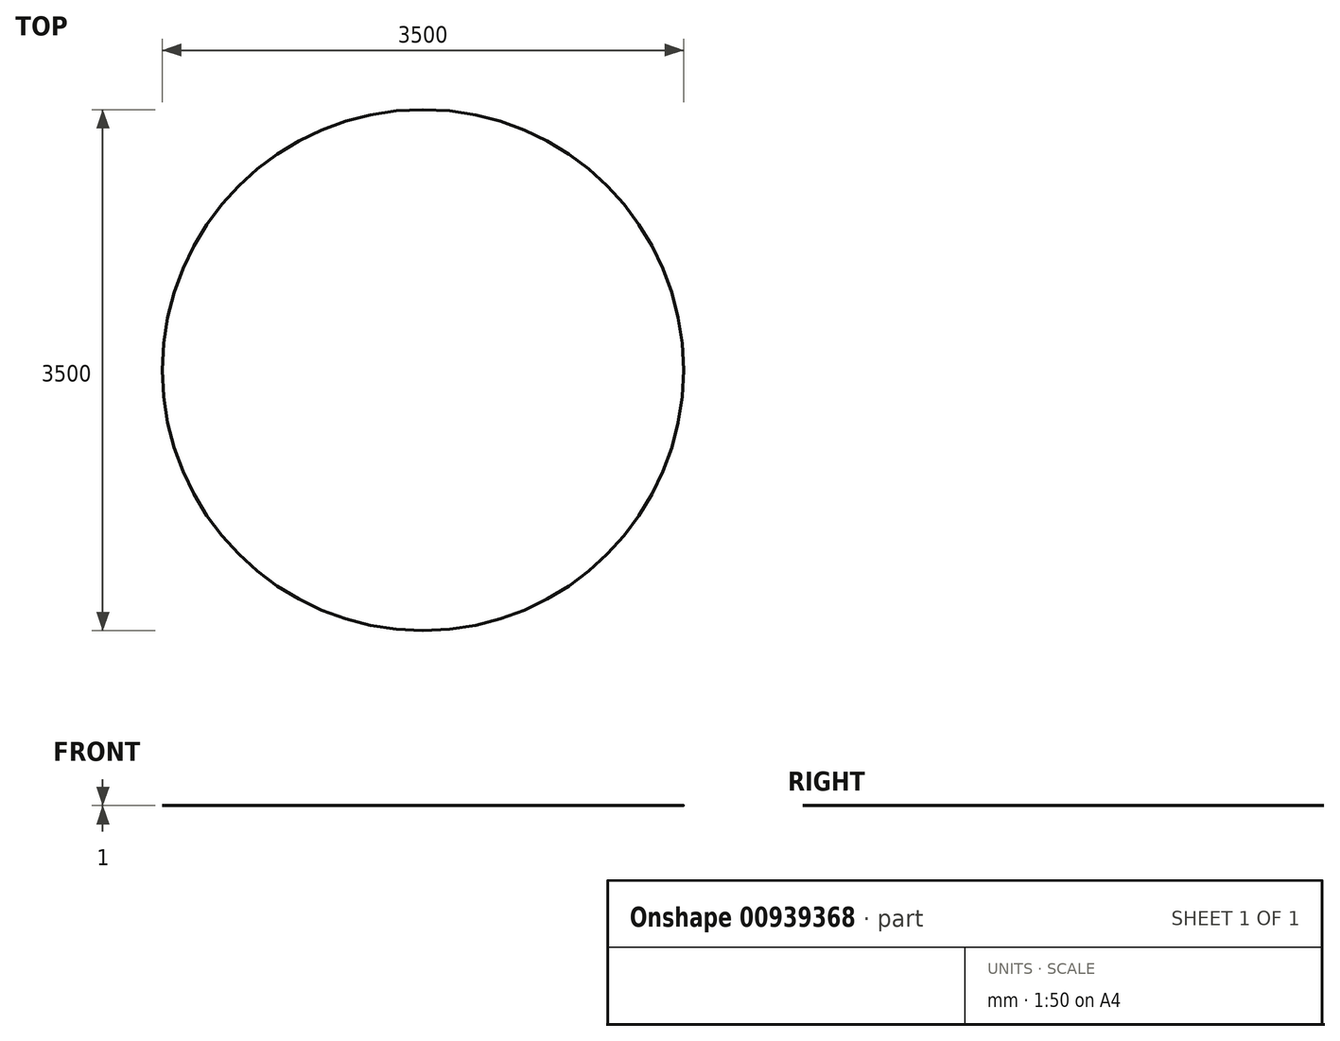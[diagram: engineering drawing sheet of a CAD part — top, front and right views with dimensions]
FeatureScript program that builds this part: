
annotation { "Feature Type Name" : "Feature", "Feature Type Description" : "" }
export const myFeature = defineFeature(function(context is Context, id is Id, definition is map)
    precondition{}
    {
        {
            var Q0;
            Q0=qCreatedBy(makeId("Top.planeOp"),FACE);
            var sketch = newSketch(context, id + "F0", { "sketchPlane" : qUnion([Q0])});
            skCircle(sketch, "E0", {"center": v(0, 0) * mm, "radius": 1750 * mm});
            skSolve(sketch);
        }
        {
            var Q0;
            Q0=makeQuery(id+"F0.imprint","IMPRINT",FACE,{"disambiguationData":[TD([[makeQuery(id+"F0.imprint","IMPRINT",EDGE,{"derivedFrom":sQuery(id+"F0.wireOp",EDGE,"E0")}),1.0]])]});
            extrude(context, id + "F1", {"entities" : qUnion([Q0]), "depth" : 1 * mm, "offsetDistance" : 25 * mm});
        }
    });
